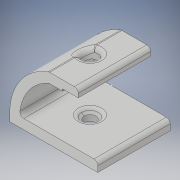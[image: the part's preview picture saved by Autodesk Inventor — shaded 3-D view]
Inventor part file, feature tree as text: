
AUTODESK INVENTOR PART (.ipt)
format: ipt  version: 2019 (Build 230136000, 136)  size: 470,528 bytes
history: native  units: mm
features: fillet x6, sketch x5, extrude x4
ambient origin geometry x8: Origin, YZ Plane, XZ Plane, XY Plane, X Axis, Y Axis, Z Axis, Center Point
bodies: Solid1 (feature_tree)
feature tree (15):
  sketch  "Sketch1"  dims[d2=45.0mm d3=5.0mm]
  extrude  "Extrusion1"  Depth=45.0mm
  extrude  "Extrusion2"  Depth=37.0mm TaperAngle=0.0deg
  fillet  "Fillet1"  Radius=8.0mm
  fillet  "Fillet2"  Radius=37.0mm
  extrude  "Extrusion3"  Depth=3.0mm
  fillet  "Fillet3"  Radius=8.0mm
  fillet  "Fillet4"  Radius=6.0mm
  fillet  "Fillet5"  Radius=3.0mm
  fillet  "Fillet6"  Radius=2.0mm
  extrude  "Extrusion4"  Depth=2.0mm
  sketch  "Sketch2"  dims[d14=8.0mm d15=37.0mm d16=0.0mm d18=8.0mm d19=37.0mm d20=0.0mm]
  sketch  "Sketch3"  dims[d21=2.0mm d22=2.0mm d26=8.0mm d27=6.0mm d28=3.0mm d29=0.0mm d30=2.0mm]
  sketch  "Sketch5"  dims[d31=2.0mm d32=2.0mm]
  sketch  "Sketch6"  dims[d33=2.0mm d34=1.0mm d35=0.0mm]
